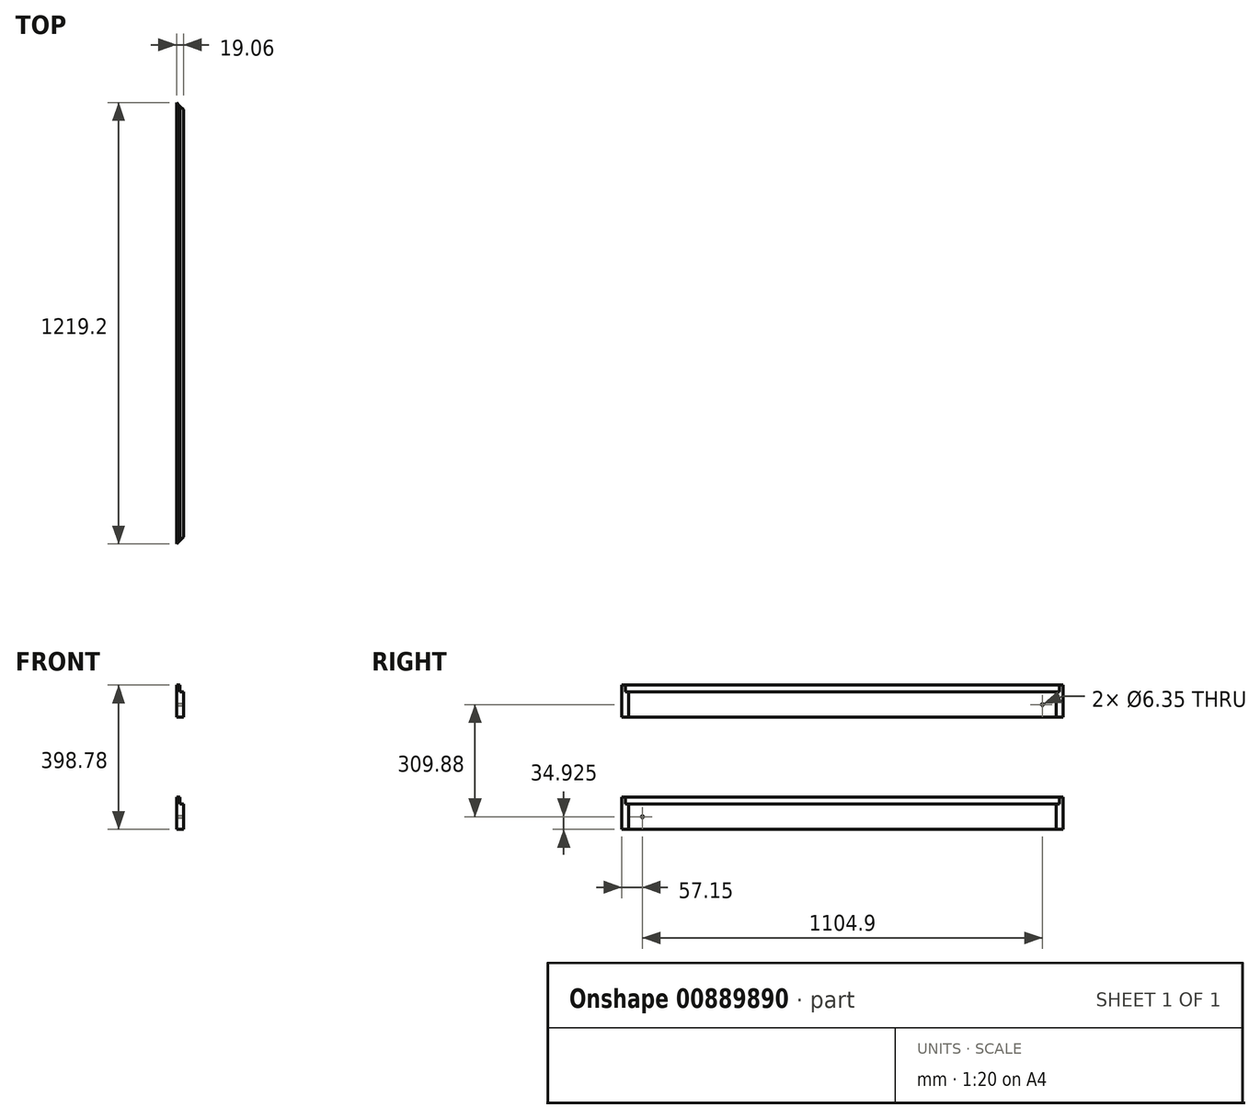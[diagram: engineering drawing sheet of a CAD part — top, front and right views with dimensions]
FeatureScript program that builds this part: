
annotation { "Feature Type Name" : "Feature", "Feature Type Description" : "" }
export const myFeature = defineFeature(function(context is Context, id is Id, definition is map)
    precondition{}
    {
        {
            var Q0;
            Q0=qCreatedBy(makeId("Front.planeOp"),FACE);
            var sketch = newSketch(context, id + "F0", { "sketchPlane" : qUnion([Q0])});
            skLineSegment(sketch, "E0.bottom", {"start": v(9.53, -44.45) * mm, "end": v(-9.53, -44.45) * mm});
            skLineSegment(sketch, "E0.top", {"start": v(9.53, 44.45) * mm, "end": v(-9.53, 44.45) * mm});
            skLineSegment(sketch, "E0.left", {"start": v(9.53, -44.45) * mm, "end": v(9.53, 44.45) * mm});
            skLineSegment(sketch, "E0.right", {"start": v(-9.53, -44.45) * mm, "end": v(-9.53, 44.45) * mm});
            skPoint(sketch, "E0.middle", {"position": v(0, 0) * mm});
            skSolve(sketch);
        }
        {
            var Q0;
            Q0 = qSketchRegion(id + "F0", true);
            extrude(context, id + "F1", {"entities" : qUnion([Q0]), "depth" : 1219.2 * mm, "offsetDistance" : 25.4 * mm});
        }
        {
            var Q0;
            Q0=makeQuery(id+"F1.opExtrude","SWEPT_FACE",FACE,{"disambiguationData":[OSD([sQuery(id+"F0.wireOp",EDGE,"E0.top")])]});
            var sketch = newSketch(context, id + "F2", { "sketchPlane" : qUnion([Q0])});
            skLineSegment(sketch, "E1", {"start": v(-9.53, -1219.2) * mm, "end": v(9.53, -1219.2) * mm});
            skLineSegment(sketch, "E2", {"start": v(9.53, -1219.2) * mm, "end": v(9.53, -1200.15) * mm});
            skLineSegment(sketch, "E3", {"start": v(9.52, -1200.15) * mm, "end": v(-9.53, -1219.2) * mm});
            skLineSegment(sketch, "E4", {"start": v(-9.53, 0) * mm, "end": v(9.53, 0) * mm});
            skLineSegment(sketch, "E5", {"start": v(9.53, 0) * mm, "end": v(9.53, -19.05) * mm});
            skLineSegment(sketch, "E6", {"start": v(9.53, -19.05) * mm, "end": v(-9.53, 0) * mm});
            skLineSegment(sketch, "E7", {"start": v(0, -1219.2) * mm, "end": v(9.53, -1219.2) * mm});
            skLineSegment(sketch, "E8", {"start": v(9.53, 0) * mm, "end": v(0, 0) * mm});
            skSolve(sketch);
        }
        {
            var Q0;
            Q0 = qSketchRegion(id + "F2", true);
            extrude(context, id + "F3", {"entities" : qUnion([Q0]), "operationType" : NewBodyOperationType.REMOVE, "endBound" : BoundingType.THROUGH_ALL, "oppositeDirection" : true, "depth" : 25.4 * mm, "offsetDistance" : 25.4 * mm});
        }
        {
            var Q0;
            Q0=makeQuery(id+"F1.opExtrude","SWEPT_FACE",FACE,{"disambiguationData":[OSD([sQuery(id+"F0.wireOp",EDGE,"E0.top")])]});
            var sketch = newSketch(context, id + "F4", { "sketchPlane" : qUnion([Q0])});
            skLineSegment(sketch, "E9", {"start": v(0, -1209.67) * mm, "end": v(9.52, -1200.15) * mm});
            skLineSegment(sketch, "E10", {"start": v(9.53, -1200.15) * mm, "end": v(9.53, -19.05) * mm});
            skLineSegment(sketch, "E11", {"start": v(9.53, -19.05) * mm, "end": v(0, -9.53) * mm});
            skLineSegment(sketch, "E12", {"start": v(0, -9.53) * mm, "end": v(0, -1209.67) * mm});
            skSolve(sketch);
        }
        {
            var Q0;
            Q0=makeQuery(id+"F4.imprint","IMPRINT",FACE,{"disambiguationData":[TD([[makeQuery(id+"F4.imprint","IMPRINT",EDGE,{"derivedFrom":sQuery(id+"F4.wireOp",EDGE,"E9")}),-1.0]])]});
            extrude(context, id + "F5", {"entities" : qUnion([Q0]), "operationType" : NewBodyOperationType.REMOVE, "oppositeDirection" : true, "depth" : 19.05 * mm, "offsetDistance" : 25.4 * mm});
        }
        {
            var Q0;
            Q0=makeQuery(id+"F1.opExtrude","SWEPT_BODY",BODY,{"disambiguationData":[OSD([sQuery(id+"F0.wireOp",EDGE,"E0.bottom"),sQuery(id+"F0.wireOp",EDGE,"E0.top"),sQuery(id+"F0.wireOp",EDGE,"E0.left"),sQuery(id+"F0.wireOp",EDGE,"E0.right")])]});
            transform(context, id + "F6", {"entities" : qUnion([Q0]), "transformType" : TransformType.TRANSLATION_3D, "dx" : 0 * mm, "dy" : 0 * mm, "dz" : 309.88 * mm, "makeCopy" : true});
        }
        {
            var Q0;
            Q0=makeQuery(id+"F6.opPattern","COPY",FACE,{"derivedFrom":makeQuery(id+"F1.opExtrude","SWEPT_FACE",FACE,{"disambiguationData":[OSD([sQuery(id+"F0.wireOp",EDGE,"E0.left")])]}),"instanceName":"1"});
            var sketch = newSketch(context, id + "F7", { "sketchPlane" : qUnion([Q0])});
            skLineSegment(sketch, "E13", {"start": v(-19.05, 300.35) * mm, "end": v(-57.15, 300.35) * mm, "construction": true});
            skSolve(sketch);
        }
        {
            var Q0;
            Q0=sQuery(id+"F7.wireOp",VERTEX,"E13.end");
            var Q1;
            Q1=makeQuery(id+"F6.opPattern","COPY",BODY,{"derivedFrom":makeQuery(id+"F1.opExtrude","SWEPT_BODY",BODY,{"disambiguationData":[OSD([sQuery(id+"F0.wireOp",EDGE,"E0.bottom"),sQuery(id+"F0.wireOp",EDGE,"E0.top"),sQuery(id+"F0.wireOp",EDGE,"E0.left"),sQuery(id+"F0.wireOp",EDGE,"E0.right")])]}),"instanceName":"1"});
            hole(context, id + "F8", {"style" : HoleStyle.SIMPLE, "endStyle" : HoleEndStyle.THROUGH, "holeDiameter" : 6.35 * mm, "majorDiameter" : 6.35 * mm, "isTappedThrough" : true, "tappedDepth" : 12.7 * mm, "tapClearance" : 3, "locations" : qUnion([Q0]), "scope" : qUnion([Q1])});
        }
        {
            var Q0;
            Q0=makeQuery(id+"F1.opExtrude","SWEPT_FACE",FACE,{"disambiguationData":[OSD([sQuery(id+"F0.wireOp",EDGE,"E0.left")])]});
            var sketch = newSketch(context, id + "F9", { "sketchPlane" : qUnion([Q0])});
            skLineSegment(sketch, "E14", {"start": v(-1200.15, -9.53) * mm, "end": v(-1162.05, -9.53) * mm, "construction": true});
            skSolve(sketch);
        }
        {
            var Q0;
            Q0=sQuery(id+"F9.wireOp",VERTEX,"E14.end");
            var Q1;
            Q1=makeQuery(id+"F1.opExtrude","SWEPT_BODY",BODY,{"disambiguationData":[OSD([sQuery(id+"F0.wireOp",EDGE,"E0.bottom"),sQuery(id+"F0.wireOp",EDGE,"E0.top"),sQuery(id+"F0.wireOp",EDGE,"E0.left"),sQuery(id+"F0.wireOp",EDGE,"E0.right")])]});
            hole(context, id + "F10", {"style" : HoleStyle.SIMPLE, "endStyle" : HoleEndStyle.THROUGH, "holeDiameter" : 6.35 * mm, "majorDiameter" : 6.35 * mm, "isTappedThrough" : true, "tappedDepth" : 12.7 * mm, "tapClearance" : 3, "locations" : qUnion([Q0]), "scope" : qUnion([Q1])});
        }
    });
